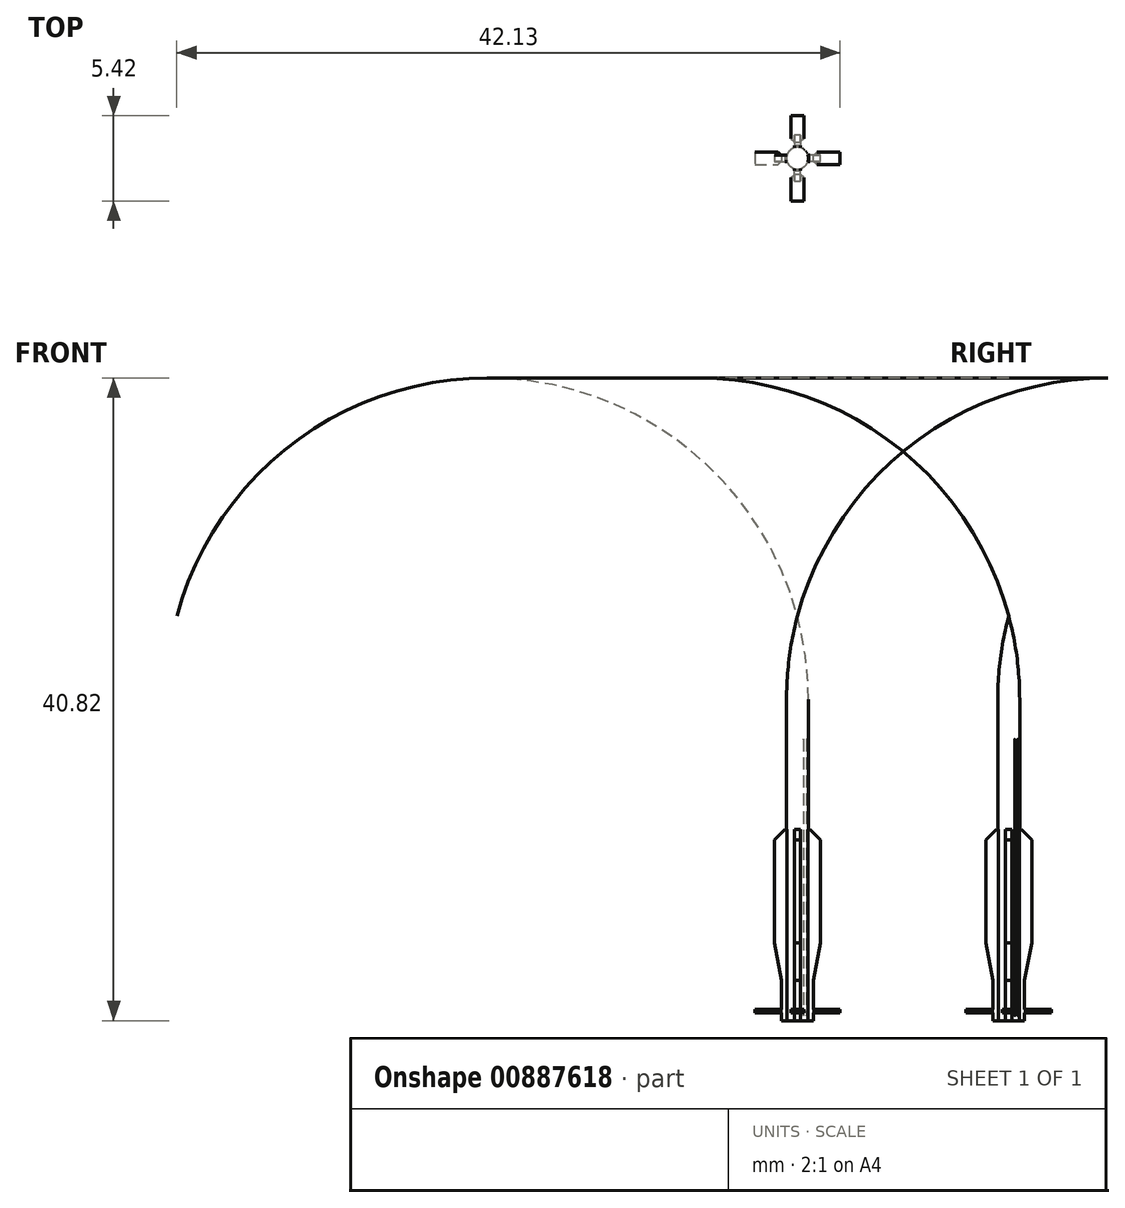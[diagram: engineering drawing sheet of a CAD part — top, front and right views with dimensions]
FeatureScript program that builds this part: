
annotation { "Feature Type Name" : "Feature", "Feature Type Description" : "" }
export const myFeature = defineFeature(function(context is Context, id is Id, definition is map)
    precondition{}
    {
        {
            assignVariable(context, id + "F0", {"name" : "s", "anyValue" : 144});
        }
        {
            var Q0;
            Q0=qCreatedBy(makeId("Front.planeOp"),FACE);
            var sketch = newSketch(context, id + "F1", { "sketchPlane" : qUnion([Q0])});
            skLineSegment(sketch, "E0", {"start": v(0, 0) * mm, "end": v(0, 25.7) * mm});
            skLineSegment(sketch, "E1", {"start": v(0.7, 20.42) * mm, "end": v(0.7, 0) * mm});
            skLineSegment(sketch, "E2", {"start": v(0.7, 0) * mm, "end": v(0, 0) * mm});
            skArc(sketch, "E3", {"start": v(0.7, 20.42) * mm, "mid": v(0.52, 23.08) * mm, "end": v(0, 25.7) * mm});
            skSolve(sketch);
        }
        {
            var Q0;
            {var subQ0=sQuery(id+"F1.wireOp",EDGE,"mrwio9nY-PsAZ-Zbfy-NhIU-sYq0QVbgGXAG");Q0=makeQuery(id+"F1.imprint","IMPRINT",FACE,{"disambiguationData":[TD([[makeQuery(id+"F1.imprint","IMPRINT",EDGE,{"derivedFrom":subQ0}),-1.0]])]});}
            var Q1;
            {var subQ7=sQuery(id+"F1.wireOp",EDGE,"E0");Q1=makeQuery(id+"F1.imprint","IMPRINT",FACE,{"disambiguationData":[TD([[makeQuery(id+"F1.imprint","IMPRINT",EDGE,{"derivedFrom":subQ7}),-1.0]])]});}
            var Q2;
            Q2=sQuery(id+"F1.wireOp",EDGE,"E0");
            revolve(context, id + "F2", {"surfaceOperationType" : NewSurfaceOperationType.NEW, "entities" : qUnion([Q0, Q1]), "axis" : qUnion([Q2]), "revolveType" : RevolveType.FULL});
        }
        {
            var Q0;
            Q0=qCreatedBy(makeId("Front.planeOp"),FACE);
            var sketch = newSketch(context, id + "F3", { "sketchPlane" : qUnion([Q0])});
            skLineSegment(sketch, "E4", {"start": v(0, 0) * mm, "end": v(0, 12.15) * mm});
            skLineSegment(sketch, "E5", {"start": v(2.7, 0.73) * mm, "end": v(2.7, 0.49) * mm});
            skLineSegment(sketch, "E6", {"start": v(0.7, 0) * mm, "end": v(0.7, 32.87) * mm, "construction": true});
            skLineSegment(sketch, "E7", {"start": v(2.7, 0.49) * mm, "end": v(1, 0.49) * mm});
            skLineSegment(sketch, "E8.0", {"start": v(0.7, 0) * mm, "end": v(-0.7, 0) * mm});
            skLineSegment(sketch, "E9", {"start": v(1.46, 11.5) * mm, "end": v(0.8, 12.15) * mm});
            skPoint(sketch, "E10", {"position": v(0.7, 5.62) * mm});
            skLineSegment(sketch, "E11", {"start": v(0, 0) * mm, "end": v(1, 0) * mm});
            skLineSegment(sketch, "E12", {"start": v(1, 0) * mm, "end": v(1, 0.49) * mm});
            skLineSegment(sketch, "E13", {"start": v(1, 2.57) * mm, "end": v(1.46, 4.93) * mm});
            skLineSegment(sketch, "E14", {"start": v(1.46, 4.93) * mm, "end": v(1.46, 11.5) * mm});
            skLineSegment(sketch, "E15.trimOffspring", {"start": v(1, 0.73) * mm, "end": v(2.7, 0.73) * mm});
            skLineSegment(sketch, "E16.trimOffspring", {"start": v(1, 0.73) * mm, "end": v(1, 2.57) * mm});
            skLineSegment(sketch, "E17", {"start": v(0.8, 12.15) * mm, "end": v(0, 12.15) * mm});
            skSolve(sketch);
        }
        {
            var Q0;
            Q0=qSketchRegion(id+"F3",true);
            extrude(context, id + "F4", {"entities" : qUnion([Q0]), "operationType" : NewBodyOperationType.ADD, "depth" : .4 * mm, "offsetDistance" : 25 * mm, "symmetric" : true});
        }
        {
            var Q0;
            Q0=makeQuery(id+"F4.opExtrude","SWEPT_FACE",FACE,{"disambiguationData":[OSD([sQuery(id+"F3.wireOp",EDGE,"E7")])]});
            var Q1;
            Q1=makeQuery(id+"F4.opExtrude","SWEPT_FACE",FACE,{"disambiguationData":[OSD([sQuery(id+"F3.wireOp",EDGE,"E7")])]});
            var sketch = newSketch(context, id + "F5", { "sketchPlane" : qUnion([Q0, Q1])});
            skLineSegment(sketch, "E18.bottom", {"start": v(2.7, -0.4) * mm, "end": v(1.25, -0.4) * mm});
            skLineSegment(sketch, "E18.top", {"start": v(2.7, 0.4) * mm, "end": v(1.25, 0.4) * mm});
            skLineSegment(sketch, "E18.left", {"start": v(2.7, -0.4) * mm, "end": v(2.7, 0.4) * mm});
            skLineSegment(sketch, "E18.right", {"start": v(1.25, -0.4) * mm, "end": v(1.25, 0.4) * mm});
            skLineSegment(sketch, "E19", {"start": v(0, 0) * mm, "end": v(1.25, 0) * mm});
            skSolve(sketch);
        }
        {
            var Q0;
            Q0=qSketchRegion(id+"F5",true);
            var Q1;
            Q1=makeQuery(id+"F4.opExtrude","SWEPT_FACE",FACE,{"disambiguationData":[OSD([sQuery(id+"F3.wireOp",EDGE,"E15.trimOffspring")])]});
            extrude(context, id + "F6", {"entities" : qUnion([Q0]), "operationType" : NewBodyOperationType.ADD, "endBound" : BoundingType.UP_TO_SURFACE, "oppositeDirection" : true, "depth" : 25 * mm, "endBoundEntityFace" : qUnion([Q1]), "offsetDistance" : 25 * mm});
        }
        {
            var Q0;
            Q0=makeQuery(id+"F2.opRevolve","SWEPT_BODY",BODY,{"disambiguationData":[OSD([sQuery(id+"F1.wireOp",EDGE,"E0"),sQuery(id+"F1.wireOp",EDGE,"E1"),sQuery(id+"F1.wireOp",EDGE,"E2"),sQuery(id+"F1.wireOp",EDGE,"2EiOItwe-9FNA-eY8p-DkXH-AMy5AHyUmzZA"),sQuery(id+"F1.wireOp",EDGE,"E3")])]});
            var Q1;
            Q1=makeQuery(id+"F2.opRevolve","SWEPT_FACE",FACE,{"disambiguationData":[OSD([sQuery(id+"F1.wireOp",EDGE,"E1")])]});
            circularPattern(context, id + "F7", {"operationType" : NewBodyOperationType.ADD, "entities" : qUnion([Q0]), "axis" : qUnion([Q1]), "angle" : 360 * degree, "instanceCount" : 4, "equalSpace" : true, "computeTransformsWithoutBuiltin" : true});
        }
        {
            var Q0;
            Q0=qCreatedBy(makeId("Top.planeOp"),FACE);
            cPlane(context, id + "F8", {"entities" : qUnion([Q0]), "cplaneType" : CPlaneType.OFFSET, "offset" : (75 / getVariable(context, 's')) * mm, "width" : 150 * mm, "height" : 150 * mm});
        }
        {
            var Q0;
            Q0=qCreatedBy(id+"F8.planeOp",FACE);
            var sketch = newSketch(context, id + "F9", { "sketchPlane" : qUnion([Q0])});
            skLineSegment(sketch, "E20", {"start": v(-0.06, -0.25) * mm, "end": v(-0.25, -0.06) * mm});
            skLineSegment(sketch, "E21", {"start": v(0.4, 0.59) * mm, "end": v(-0.25, -0.06) * mm});
            skLineSegment(sketch, "E22", {"start": v(-0.06, -0.25) * mm, "end": v(0.59, 0.4) * mm});
            skLineSegment(sketch, "E23", {"start": v(0, -0.45) * mm, "end": v(0, 0) * mm, "construction": true});
            skLineSegment(sketch, "E24", {"start": v(0, 0) * mm, "end": v(-0.16, -0.16) * mm, "construction": true});
            skArc(sketch, "E25", {"start": v(0.4, 0.59) * mm, "mid": v(0.4, 0.4) * mm, "end": v(0.59, 0.4) * mm});
            skSolve(sketch);
        }
        {
            var Q0;
            Q0=qSketchRegion(id+"F9",true);
            extrude(context, id + "F10", {"entities" : qUnion([Q0]), "operationType" : NewBodyOperationType.ADD, "depth" : (2500 / getVariable(context, 's')) * mm, "offsetDistance" : 25 * mm});
        }
        {
            var Q0;
            Q0=makeQuery(id+"F10.boolean.opBoolean","INTERSECT",EDGE,{"derivedFrom":[makeQuery(id+"F2.opRevolve","SWEPT_FACE",FACE,{"disambiguationData":[OSD([sQuery(id+"F1.wireOp",EDGE,"E1")])]}),makeQuery(id+"F10.opExtrude","CAP_FACE",FACE,{"disambiguationData":[OSD([sQuery(id+"F9.wireOp",EDGE,"E20"),sQuery(id+"F9.wireOp",EDGE,"E21"),sQuery(id+"F9.wireOp",EDGE,"E22"),sQuery(id+"F9.wireOp",EDGE,"E25")])],"isStart":true})]});
            chamfer(context, id + "F11", {"entities" : qUnion([Q0]), "width" : .2 * mm, "tangentPropagation" : true});
        }
        {
            var Q0;
            Q0=makeQuery(id+"F10.opExtrude","CAP_EDGE",EDGE,{"disambiguationData":[OSD([sQuery(id+"F9.wireOp",EDGE,"E25")])],"isStart":false});
            fillet(context, id + "F12", {"entities" : qUnion([Q0]), "radius" : (20 / getVariable(context, 's')) * mm, "tangentPropagation" : true, "allowEdgeOverflow" : false});
        }
        {
            var Q0;
            {var subQ0=sQuery(id+"F3.wireOp",EDGE,"oVrJ5IzZ-ahxD-dP88-c25y-iCYn6jxEnnUr");var subQ1=sQuery(id+"F3.wireOp",EDGE,"E5");var subQ2=sQuery(id+"F3.wireOp",EDGE,"E7");Q0=makeQuery(id+"F6.boolean.opBoolean","INTERSECT",EDGE,{"derivedFrom":[makeQuery(id+"F4.boolean.opBoolean","SPLIT",FACE,{"disambiguationData":[TD([makeQuery(id+"F4.opExtrude","SWEPT_FACE",FACE,{"disambiguationData":[OSD([subQ0])]})])],"derivedFrom":makeQuery(id+"F4.opExtrude","CAP_FACE",FACE,{"disambiguationData":[OSD([sQuery(id+"F3.wireOp",EDGE,"E4"),sQuery(id+"F3.wireOp",EDGE,"wy9EaCHD-QEEi-l8sX-yeaH-TlzYOR0AgPI2"),subQ0,subQ1,subQ2,sQuery(id+"F3.wireOp",EDGE,"KvtmA3p7-kHr7-HYAJ-nlAS-aqGmsH8HB3TV"),sQuery(id+"F3.wireOp",EDGE,"p5XcWhG3-a5s5-I4K6-10Ig-DutLYPjUeVzo"),sQuery(id+"F3.wireOp",EDGE,"E9")])],"isStart":false})}),makeQuery(id+"F6.opExtrude","SWEPT_FACE",FACE,{"disambiguationData":[OSD([sQuery(id+"F5.wireOp",EDGE,"E18.right")])]})]});}
            var Q1;
            {var subQ0=sQuery(id+"F3.wireOp",EDGE,"oVrJ5IzZ-ahxD-dP88-c25y-iCYn6jxEnnUr");var subQ1=sQuery(id+"F3.wireOp",EDGE,"E5");var subQ2=sQuery(id+"F3.wireOp",EDGE,"E7");Q1=makeQuery(id+"F6.boolean.opBoolean","INTERSECT",EDGE,{"derivedFrom":[makeQuery(id+"F4.boolean.opBoolean","SPLIT",FACE,{"disambiguationData":[TD([makeQuery(id+"F4.opExtrude","SWEPT_FACE",FACE,{"disambiguationData":[OSD([subQ0])]})])],"derivedFrom":makeQuery(id+"F4.opExtrude","CAP_FACE",FACE,{"disambiguationData":[OSD([sQuery(id+"F3.wireOp",EDGE,"E4"),sQuery(id+"F3.wireOp",EDGE,"wy9EaCHD-QEEi-l8sX-yeaH-TlzYOR0AgPI2"),subQ0,subQ1,subQ2,sQuery(id+"F3.wireOp",EDGE,"KvtmA3p7-kHr7-HYAJ-nlAS-aqGmsH8HB3TV"),sQuery(id+"F3.wireOp",EDGE,"p5XcWhG3-a5s5-I4K6-10Ig-DutLYPjUeVzo"),sQuery(id+"F3.wireOp",EDGE,"E9")])],"isStart":true})}),makeQuery(id+"F6.opExtrude","SWEPT_FACE",FACE,{"disambiguationData":[OSD([sQuery(id+"F5.wireOp",EDGE,"E18.right")])]})]});}
            var Q2;
            {var subQ0=sQuery(id+"F3.wireOp",EDGE,"oVrJ5IzZ-ahxD-dP88-c25y-iCYn6jxEnnUr");var subQ1=sQuery(id+"F3.wireOp",EDGE,"E5");var subQ2=sQuery(id+"F3.wireOp",EDGE,"E7");Q2=makeQuery(id+"F7.opPattern","COPY",EDGE,{"derivedFrom":makeQuery(id+"F6.boolean.opBoolean","INTERSECT",EDGE,{"derivedFrom":[makeQuery(id+"F4.boolean.opBoolean","SPLIT",FACE,{"disambiguationData":[TD([makeQuery(id+"F4.opExtrude","SWEPT_FACE",FACE,{"disambiguationData":[OSD([subQ0])]})])],"derivedFrom":makeQuery(id+"F4.opExtrude","CAP_FACE",FACE,{"disambiguationData":[OSD([sQuery(id+"F3.wireOp",EDGE,"E4"),sQuery(id+"F3.wireOp",EDGE,"wy9EaCHD-QEEi-l8sX-yeaH-TlzYOR0AgPI2"),subQ0,subQ1,subQ2,sQuery(id+"F3.wireOp",EDGE,"KvtmA3p7-kHr7-HYAJ-nlAS-aqGmsH8HB3TV"),sQuery(id+"F3.wireOp",EDGE,"p5XcWhG3-a5s5-I4K6-10Ig-DutLYPjUeVzo"),sQuery(id+"F3.wireOp",EDGE,"E9")])],"isStart":false})}),makeQuery(id+"F6.opExtrude","SWEPT_FACE",FACE,{"disambiguationData":[OSD([sQuery(id+"F5.wireOp",EDGE,"E18.right")])]})]}),"instanceName":"3"});}
            var Q3;
            {var subQ0=sQuery(id+"F3.wireOp",EDGE,"oVrJ5IzZ-ahxD-dP88-c25y-iCYn6jxEnnUr");var subQ1=sQuery(id+"F3.wireOp",EDGE,"E5");var subQ2=sQuery(id+"F3.wireOp",EDGE,"E7");Q3=makeQuery(id+"F7.opPattern","COPY",EDGE,{"derivedFrom":makeQuery(id+"F6.boolean.opBoolean","INTERSECT",EDGE,{"derivedFrom":[makeQuery(id+"F4.boolean.opBoolean","SPLIT",FACE,{"disambiguationData":[TD([makeQuery(id+"F4.opExtrude","SWEPT_FACE",FACE,{"disambiguationData":[OSD([subQ0])]})])],"derivedFrom":makeQuery(id+"F4.opExtrude","CAP_FACE",FACE,{"disambiguationData":[OSD([sQuery(id+"F3.wireOp",EDGE,"E4"),sQuery(id+"F3.wireOp",EDGE,"wy9EaCHD-QEEi-l8sX-yeaH-TlzYOR0AgPI2"),subQ0,subQ1,subQ2,sQuery(id+"F3.wireOp",EDGE,"KvtmA3p7-kHr7-HYAJ-nlAS-aqGmsH8HB3TV"),sQuery(id+"F3.wireOp",EDGE,"p5XcWhG3-a5s5-I4K6-10Ig-DutLYPjUeVzo"),sQuery(id+"F3.wireOp",EDGE,"E9")])],"isStart":true})}),makeQuery(id+"F6.opExtrude","SWEPT_FACE",FACE,{"disambiguationData":[OSD([sQuery(id+"F5.wireOp",EDGE,"E18.right")])]})]}),"instanceName":"3"});}
            var Q4;
            {var subQ0=sQuery(id+"F3.wireOp",EDGE,"oVrJ5IzZ-ahxD-dP88-c25y-iCYn6jxEnnUr");var subQ1=sQuery(id+"F3.wireOp",EDGE,"E5");var subQ2=sQuery(id+"F3.wireOp",EDGE,"E7");Q4=makeQuery(id+"F7.opPattern","COPY",EDGE,{"derivedFrom":makeQuery(id+"F6.boolean.opBoolean","INTERSECT",EDGE,{"derivedFrom":[makeQuery(id+"F4.boolean.opBoolean","SPLIT",FACE,{"disambiguationData":[TD([makeQuery(id+"F4.opExtrude","SWEPT_FACE",FACE,{"disambiguationData":[OSD([subQ0])]})])],"derivedFrom":makeQuery(id+"F4.opExtrude","CAP_FACE",FACE,{"disambiguationData":[OSD([sQuery(id+"F3.wireOp",EDGE,"E4"),sQuery(id+"F3.wireOp",EDGE,"wy9EaCHD-QEEi-l8sX-yeaH-TlzYOR0AgPI2"),subQ0,subQ1,subQ2,sQuery(id+"F3.wireOp",EDGE,"KvtmA3p7-kHr7-HYAJ-nlAS-aqGmsH8HB3TV"),sQuery(id+"F3.wireOp",EDGE,"p5XcWhG3-a5s5-I4K6-10Ig-DutLYPjUeVzo"),sQuery(id+"F3.wireOp",EDGE,"E9")])],"isStart":false})}),makeQuery(id+"F6.opExtrude","SWEPT_FACE",FACE,{"disambiguationData":[OSD([sQuery(id+"F5.wireOp",EDGE,"E18.right")])]})]}),"instanceName":"2"});}
            var Q5;
            {var subQ0=sQuery(id+"F3.wireOp",EDGE,"oVrJ5IzZ-ahxD-dP88-c25y-iCYn6jxEnnUr");var subQ1=sQuery(id+"F3.wireOp",EDGE,"E5");var subQ2=sQuery(id+"F3.wireOp",EDGE,"E7");Q5=makeQuery(id+"F7.opPattern","COPY",EDGE,{"derivedFrom":makeQuery(id+"F6.boolean.opBoolean","INTERSECT",EDGE,{"derivedFrom":[makeQuery(id+"F4.boolean.opBoolean","SPLIT",FACE,{"disambiguationData":[TD([makeQuery(id+"F4.opExtrude","SWEPT_FACE",FACE,{"disambiguationData":[OSD([subQ0])]})])],"derivedFrom":makeQuery(id+"F4.opExtrude","CAP_FACE",FACE,{"disambiguationData":[OSD([sQuery(id+"F3.wireOp",EDGE,"E4"),sQuery(id+"F3.wireOp",EDGE,"wy9EaCHD-QEEi-l8sX-yeaH-TlzYOR0AgPI2"),subQ0,subQ1,subQ2,sQuery(id+"F3.wireOp",EDGE,"KvtmA3p7-kHr7-HYAJ-nlAS-aqGmsH8HB3TV"),sQuery(id+"F3.wireOp",EDGE,"p5XcWhG3-a5s5-I4K6-10Ig-DutLYPjUeVzo"),sQuery(id+"F3.wireOp",EDGE,"E9")])],"isStart":true})}),makeQuery(id+"F6.opExtrude","SWEPT_FACE",FACE,{"disambiguationData":[OSD([sQuery(id+"F5.wireOp",EDGE,"E18.right")])]})]}),"instanceName":"1"});}
            var Q6;
            {var subQ0=sQuery(id+"F3.wireOp",EDGE,"oVrJ5IzZ-ahxD-dP88-c25y-iCYn6jxEnnUr");var subQ1=sQuery(id+"F3.wireOp",EDGE,"E5");var subQ2=sQuery(id+"F3.wireOp",EDGE,"E7");Q6=makeQuery(id+"F7.opPattern","COPY",EDGE,{"derivedFrom":makeQuery(id+"F6.boolean.opBoolean","INTERSECT",EDGE,{"derivedFrom":[makeQuery(id+"F4.boolean.opBoolean","SPLIT",FACE,{"disambiguationData":[TD([makeQuery(id+"F4.opExtrude","SWEPT_FACE",FACE,{"disambiguationData":[OSD([subQ0])]})])],"derivedFrom":makeQuery(id+"F4.opExtrude","CAP_FACE",FACE,{"disambiguationData":[OSD([sQuery(id+"F3.wireOp",EDGE,"E4"),sQuery(id+"F3.wireOp",EDGE,"wy9EaCHD-QEEi-l8sX-yeaH-TlzYOR0AgPI2"),subQ0,subQ1,subQ2,sQuery(id+"F3.wireOp",EDGE,"KvtmA3p7-kHr7-HYAJ-nlAS-aqGmsH8HB3TV"),sQuery(id+"F3.wireOp",EDGE,"p5XcWhG3-a5s5-I4K6-10Ig-DutLYPjUeVzo"),sQuery(id+"F3.wireOp",EDGE,"E9")])],"isStart":false})}),makeQuery(id+"F6.opExtrude","SWEPT_FACE",FACE,{"disambiguationData":[OSD([sQuery(id+"F5.wireOp",EDGE,"E18.right")])]})]}),"instanceName":"1"});}
            var Q7;
            {var subQ0=sQuery(id+"F3.wireOp",EDGE,"oVrJ5IzZ-ahxD-dP88-c25y-iCYn6jxEnnUr");var subQ1=sQuery(id+"F3.wireOp",EDGE,"E5");var subQ2=sQuery(id+"F3.wireOp",EDGE,"E7");Q7=makeQuery(id+"F7.opPattern","COPY",EDGE,{"derivedFrom":makeQuery(id+"F6.boolean.opBoolean","INTERSECT",EDGE,{"derivedFrom":[makeQuery(id+"F4.boolean.opBoolean","SPLIT",FACE,{"disambiguationData":[TD([makeQuery(id+"F4.opExtrude","SWEPT_FACE",FACE,{"disambiguationData":[OSD([subQ0])]})])],"derivedFrom":makeQuery(id+"F4.opExtrude","CAP_FACE",FACE,{"disambiguationData":[OSD([sQuery(id+"F3.wireOp",EDGE,"E4"),sQuery(id+"F3.wireOp",EDGE,"wy9EaCHD-QEEi-l8sX-yeaH-TlzYOR0AgPI2"),subQ0,subQ1,subQ2,sQuery(id+"F3.wireOp",EDGE,"KvtmA3p7-kHr7-HYAJ-nlAS-aqGmsH8HB3TV"),sQuery(id+"F3.wireOp",EDGE,"p5XcWhG3-a5s5-I4K6-10Ig-DutLYPjUeVzo"),sQuery(id+"F3.wireOp",EDGE,"E9")])],"isStart":true})}),makeQuery(id+"F6.opExtrude","SWEPT_FACE",FACE,{"disambiguationData":[OSD([sQuery(id+"F5.wireOp",EDGE,"E18.right")])]})]}),"instanceName":"2"});}
            chamfer(context, id + "F13", {"entities" : qUnion([Q0, Q1, Q2, Q3, Q4, Q5, Q6, Q7]), "width" : (30 / getVariable(context, 's')) * mm, "tangentPropagation" : true});
        }
    });
